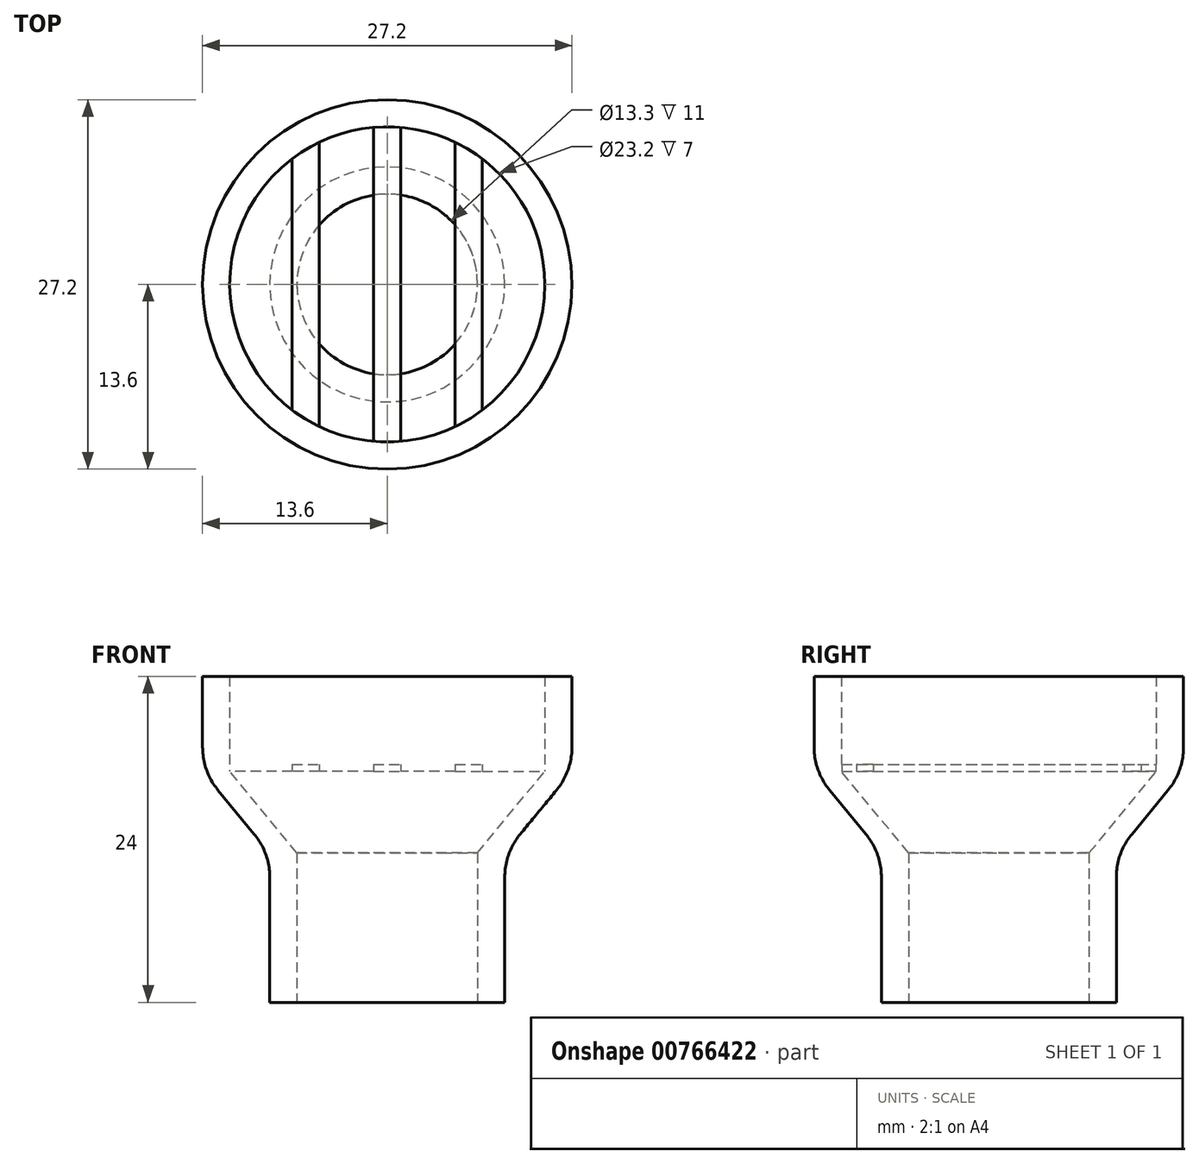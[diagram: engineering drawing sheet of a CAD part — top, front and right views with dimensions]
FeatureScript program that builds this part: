
annotation { "Feature Type Name" : "Feature", "Feature Type Description" : "" }
export const myFeature = defineFeature(function(context is Context, id is Id, definition is map)
    precondition{}
    {
        {
            var Q0;
            Q0=qCreatedBy(makeId("Top.planeOp"),FACE);
            var sketch = newSketch(context, id + "F0", { "sketchPlane" : qUnion([Q0])});
            skCircle(sketch, "E0", {"center": v(0, 0) * mm, "radius": 6.65 * mm});
            skCircle(sketch, "E1.0", {"center": v(0, 0) * mm, "radius": 8.65 * mm});
            skSolve(sketch);
        }
        {
            var Q0;
            Q0 = qSketchRegion(id + "F0", true);
            extrude(context, id + "F1", {"entities" : qUnion([Q0]), "depth" : 11 * mm, "offsetDistance" : 25 * mm});
        }
        {
            var Q0;
            Q0=qCreatedBy(makeId("Top.planeOp"),FACE);
            cPlane(context, id + "F2", {"entities" : qUnion([Q0]), "cplaneType" : CPlaneType.OFFSET, "offset" : 17 * mm, "width" : 150 * mm, "height" : 150 * mm});
        }
        {
            var Q0;
            Q0=qCreatedBy(id+"F2.planeOp",FACE);
            var sketch = newSketch(context, id + "F3", { "sketchPlane" : qUnion([Q0])});
            skCircle(sketch, "E2", {"center": v(0, 0) * mm, "radius": 11.6 * mm});
            skCircle(sketch, "E3.0", {"center": v(0, 0) * mm, "radius": 13.6 * mm});
            skSolve(sketch);
        }
        {
            var Q0;
            Q0=makeQuery(id+"F3.imprint","IMPRINT",FACE,{"disambiguationData":[TD([[makeQuery(id+"F3.imprint","IMPRINT",EDGE,{"derivedFrom":sQuery(id+"F3.wireOp",EDGE,"E2")}),-1.0]])]});
            extrude(context, id + "F4", {"entities" : qUnion([Q0]), "depth" : 7 * mm, "offsetDistance" : 25 * mm});
        }
        {
            var Q0;
            Q0=qCreatedBy(makeId("Front.planeOp"),FACE);
            var sketch = newSketch(context, id + "F5", { "sketchPlane" : qUnion([Q0])});
            skLineSegment(sketch, "E4", {"start": v(0, 0) * mm, "end": v(0, 11) * mm});
            skLineSegment(sketch, "E5", {"start": v(0, 11) * mm, "end": v(6.65, 11) * mm});
            skLineSegment(sketch, "E6", {"start": v(6.65, 11) * mm, "end": v(8.65, 11) * mm});
            skLineSegment(sketch, "E7", {"start": v(0, 11) * mm, "end": v(0, 17) * mm});
            skLineSegment(sketch, "E8", {"start": v(0, 17) * mm, "end": v(11.6, 17) * mm});
            skLineSegment(sketch, "E9", {"start": v(11.6, 17) * mm, "end": v(13.6, 17) * mm});
            skLineSegment(sketch, "E10", {"start": v(6.65, 11) * mm, "end": v(11.6, 17) * mm});
            skLineSegment(sketch, "E11", {"start": v(8.65, 11) * mm, "end": v(13.6, 17) * mm});
            skSolve(sketch);
        }
        {
            var Q0;
            Q0=makeQuery(id+"F5.imprint","IMPRINT",FACE,{"disambiguationData":[TD([[makeQuery(id+"F5.imprint","IMPRINT",EDGE,{"derivedFrom":sQuery(id+"F5.wireOp",EDGE,"E6")}),1.0]])]});
            var Q1;
            Q1=sQuery(id+"F5.wireOp",EDGE,"E7");
            revolve(context, id + "F6", {"surfaceOperationType" : NewSurfaceOperationType.NEW, "entities" : qUnion([Q0]), "axis" : qUnion([Q1]), "revolveType" : RevolveType.FULL});
        }
        {
            var Q0;
            Q0=qCreatedBy(id+"F2.planeOp",FACE);
            var sketch = newSketch(context, id + "F7", { "sketchPlane" : qUnion([Q0])});
            skCircle(sketch, "E12", {"center": v(0, 0) * mm, "radius": 12.1 * mm});
            skLineSegment(sketch, "E13", {"start": v(0, 0) * mm, "end": v(0, 12.1) * mm});
            skLineSegment(sketch, "E14", {"start": v(0, 0) * mm, "end": v(0, -12.1) * mm});
            skLineSegment(sketch, "E15", {"start": v(1, -12.06) * mm, "end": v(1, 12.06) * mm});
            skLineSegment(sketch, "E16", {"start": v(5, -11.02) * mm, "end": v(5, 11.02) * mm});
            skLineSegment(sketch, "E17", {"start": v(7, -9.87) * mm, "end": v(7, 9.87) * mm});
            skLineSegment(sketch, "E18.MirrorCS", {"start": v(-1, -12.06) * mm, "end": v(-1, 12.06) * mm});
            skLineSegment(sketch, "E19.MirrorCS", {"start": v(-5, -11.02) * mm, "end": v(-5, 11.02) * mm});
            skLineSegment(sketch, "E20.MirrorCS", {"start": v(-7, -9.87) * mm, "end": v(-7, 9.87) * mm});
            skSolve(sketch);
        }
        {
            var Q0;
            {var subQ0=sQuery(id+"F7.wireOp",EDGE,"E19.MirrorCS");Q0=makeQuery(id+"F7.imprint","IMPRINT",FACE,{"disambiguationData":[TD([[makeQuery(id+"F7.imprint","IMPRINT",EDGE,{"derivedFrom":subQ0}),1.0]])]});}
            var Q1;
            {var subQ0=sQuery(id+"F7.wireOp",EDGE,"E13");Q1=makeQuery(id+"F7.imprint","IMPRINT",FACE,{"disambiguationData":[TD([[makeQuery(id+"F7.imprint","IMPRINT",EDGE,{"derivedFrom":subQ0}),-1.0]])]});}
            var Q2;
            {var subQ1=sQuery(id+"F7.wireOp",EDGE,"E13");Q2=makeQuery(id+"F7.imprint","IMPRINT",FACE,{"disambiguationData":[TD([[makeQuery(id+"F7.imprint","IMPRINT",EDGE,{"derivedFrom":subQ1}),1.0]])]});}
            var Q3;
            {var subQ0=sQuery(id+"F7.wireOp",EDGE,"E16");Q3=makeQuery(id+"F7.imprint","IMPRINT",FACE,{"disambiguationData":[TD([[makeQuery(id+"F7.imprint","IMPRINT",EDGE,{"derivedFrom":subQ0}),-1.0]])]});}
            extrude(context, id + "F8", {"entities" : qUnion([Q0, Q1, Q2, Q3]), "depth" : .5 * mm, "offsetDistance" : 25 * mm});
        }
        {
            var Q0;
            Q0=makeQuery(id+"F1.opExtrude","SWEPT_BODY",BODY,{"disambiguationData":[OSD([sQuery(id+"F0.wireOp",EDGE,"E0"),sQuery(id+"F0.wireOp",EDGE,"E1.0")])]});
            var Q1;
            Q1=makeQuery(id+"F6.opRevolve","SWEPT_BODY",BODY,{"disambiguationData":[OSD([sQuery(id+"F5.wireOp",EDGE,"E6"),sQuery(id+"F5.wireOp",EDGE,"E9"),sQuery(id+"F5.wireOp",EDGE,"E10"),sQuery(id+"F5.wireOp",EDGE,"E11")])]});
            var Q2;
            Q2=makeQuery(id+"F4.opExtrude","SWEPT_BODY",BODY,{"disambiguationData":[OSD([sQuery(id+"F3.wireOp",EDGE,"E2"),sQuery(id+"F3.wireOp",EDGE,"E3.0")])]});
            var Q3;
            Q3=makeQuery(id+"F8.opExtrude","SWEPT_BODY",BODY,{"disambiguationData":[OSD([sQuery(id+"F7.wireOp",EDGE,"E12"),sQuery(id+"F7.wireOp",EDGE,"E16"),sQuery(id+"F7.wireOp",EDGE,"E17")])]});
            var Q4;
            Q4=makeQuery(id+"F8.opExtrude","SWEPT_BODY",BODY,{"disambiguationData":[OSD([sQuery(id+"F7.wireOp",EDGE,"E12"),sQuery(id+"F7.wireOp",EDGE,"E15"),sQuery(id+"F7.wireOp",EDGE,"E18.MirrorCS")])]});
            var Q5;
            Q5=makeQuery(id+"F8.opExtrude","SWEPT_BODY",BODY,{"disambiguationData":[OSD([sQuery(id+"F7.wireOp",EDGE,"E12"),sQuery(id+"F7.wireOp",EDGE,"E19.MirrorCS"),sQuery(id+"F7.wireOp",EDGE,"E20.MirrorCS")])]});
            booleanBodies(context, id + "F9", {"operationType" : BooleanOperationType.UNION, "tools" : qUnion([Q0, Q1, Q2, Q3, Q4, Q5])});
        }
        {
            var Q0;
            Q0=makeQuery(id+"F9.opBoolean","MERGE",EDGE,{"derivedFrom":[makeQuery(id+"F1.opExtrude","CAP_EDGE",EDGE,{"disambiguationData":[OSD([sQuery(id+"F0.wireOp",EDGE,"E1.0")])],"isStart":false}),makeQuery(id+"F6.opRevolve","SWEPT_EDGE",EDGE,{"disambiguationData":[OSD([sQuery(id+"F5.wireOp",EDGE,"E6"),sQuery(id+"F5.wireOp",EDGE,"E11")])]})]});
            var Q1;
            Q1=makeQuery(id+"F9.opBoolean","MERGE",EDGE,{"derivedFrom":[makeQuery(id+"F4.opExtrude","CAP_EDGE",EDGE,{"disambiguationData":[OSD([sQuery(id+"F3.wireOp",EDGE,"E3.0")])],"isStart":true}),makeQuery(id+"F6.opRevolve","SWEPT_EDGE",EDGE,{"disambiguationData":[OSD([sQuery(id+"F5.wireOp",EDGE,"E9"),sQuery(id+"F5.wireOp",EDGE,"E11")])]})]});
            fillet(context, id + "F10", {"entities" : qUnion([Q0, Q1]), "radius" : 5 * mm, "tangentPropagation" : true, "allowEdgeOverflow" : false});
        }
    });
